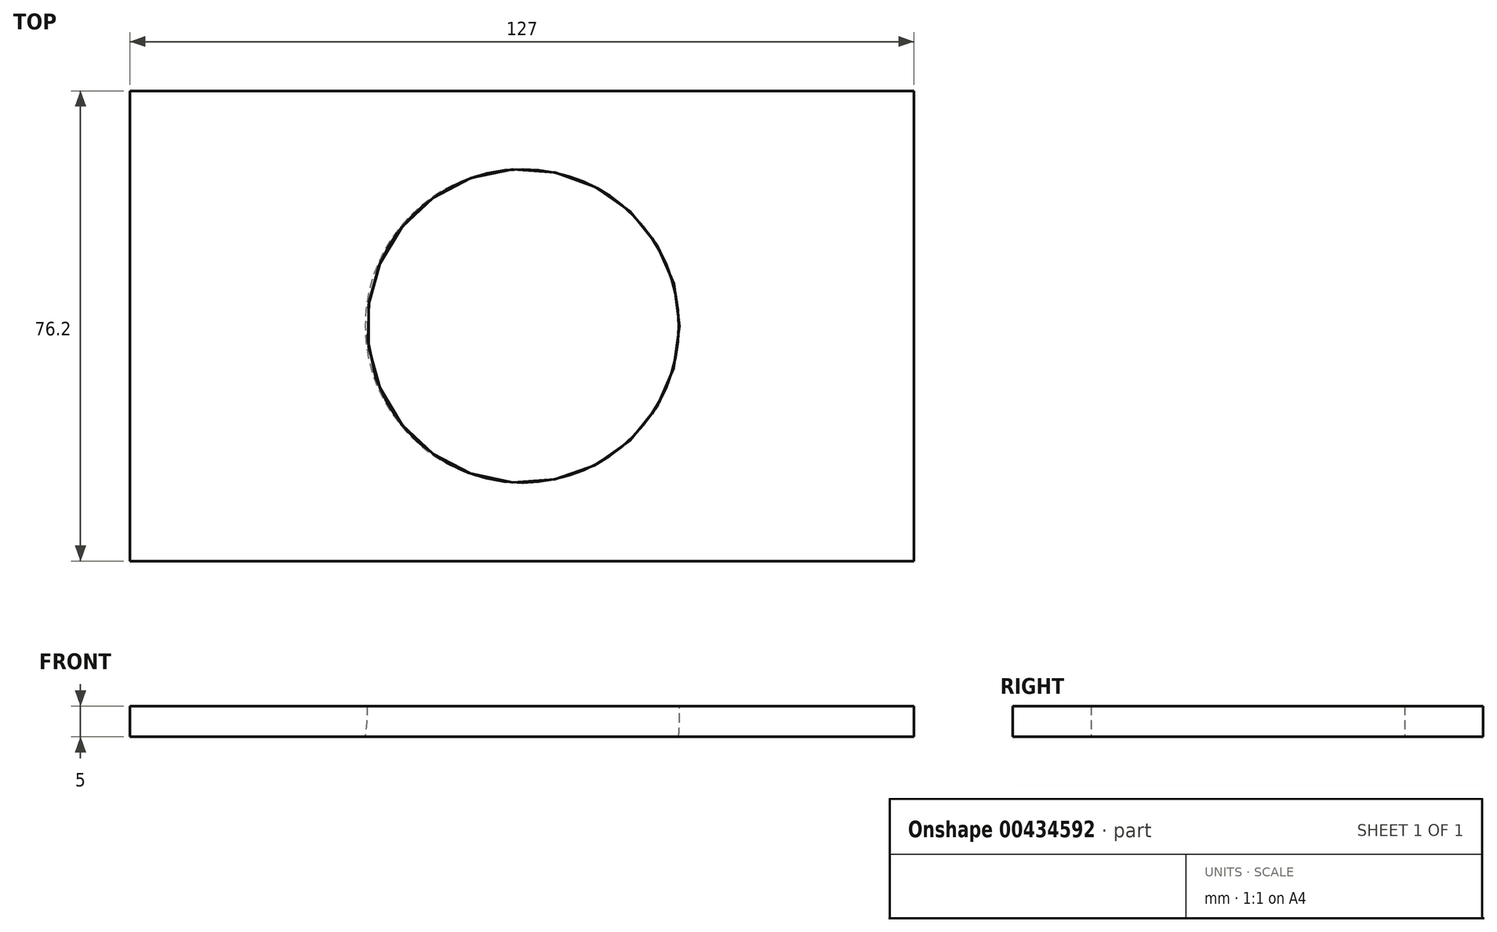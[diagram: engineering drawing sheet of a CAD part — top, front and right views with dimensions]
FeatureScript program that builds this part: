
annotation { "Feature Type Name" : "Feature", "Feature Type Description" : "" }
export const myFeature = defineFeature(function(context is Context, id is Id, definition is map)
    precondition{}
    {
        {
            var Q0;
            Q0=qCreatedBy(makeId("Top.planeOp"),FACE);
            var sketch = newSketch(context, id + "F0", { "sketchPlane" : qUnion([Q0])});
            skLineSegment(sketch, "E0.bottom", {"start": v(63.5, -38.1) * mm, "end": v(-63.5, -38.1) * mm});
            skLineSegment(sketch, "E0.top", {"start": v(63.5, 38.1) * mm, "end": v(-63.5, 38.1) * mm});
            skLineSegment(sketch, "E0.left", {"start": v(63.5, -38.1) * mm, "end": v(63.5, 38.1) * mm});
            skLineSegment(sketch, "E0.right", {"start": v(-63.5, -38.1) * mm, "end": v(-63.5, 38.1) * mm});
            skPoint(sketch, "E0.middle", {"position": v(0, 0) * mm});
            skSolve(sketch);
        }
        {
            var Q0;
            Q0 = qSketchRegion(id + "F0", true);
            extrude(context, id + "F1", {"entities" : qUnion([Q0]), "depth" : 5 * mm});
        }
        {
            var Q0;
            Q0=qCreatedBy(makeId("Top.planeOp"),FACE);
            var sketch = newSketch(context, id + "F2", { "sketchPlane" : qUnion([Q0])});
            skCircle(sketch, "E1", {"center": v(0, 0) * mm, "radius": 25.4 * mm});
            skSolve(sketch);
        }
        {
            var Q0;
            Q0 = qSketchRegion(id + "F2", true);
            var Q1;
            Q1=sQuery(id+"F2.wireOp",EDGE,"E1");
            var Q2;
            Q2=makeQuery(id+"F1.opExtrude","CAP_EDGE",EDGE,{"disambiguationData":[OSD([sQuery(id+"F0.wireOp",EDGE,"E0.right")])],"isStart":false});
            revolve(context, id + "F3", {"entities" : qUnion([Q0]), "surfaceEntities" : qUnion([Q1]), "axis" : qUnion([Q2]), "revolveType" : RevolveType.FULL});
        }
        {
            var Q0;
            Q0=makeQuery(id+"F3.opRevolve","SWEPT_BODY",BODY,{"disambiguationData":[OSD([sQuery(id+"F2.wireOp",EDGE,"E1")])]});
            var Q1;
            Q1=makeQuery(id+"F1.opExtrude","SWEPT_BODY",BODY,{"disambiguationData":[OSD([sQuery(id+"F0.wireOp",EDGE,"E0.bottom"),sQuery(id+"F0.wireOp",EDGE,"E0.top"),sQuery(id+"F0.wireOp",EDGE,"E0.left"),sQuery(id+"F0.wireOp",EDGE,"E0.right")])]});
            booleanBodies(context, id + "F4", {"operationType" : BooleanOperationType.SUBTRACTION, "tools" : qUnion([Q0]), "targets" : qUnion([Q1])});
        }
    });
